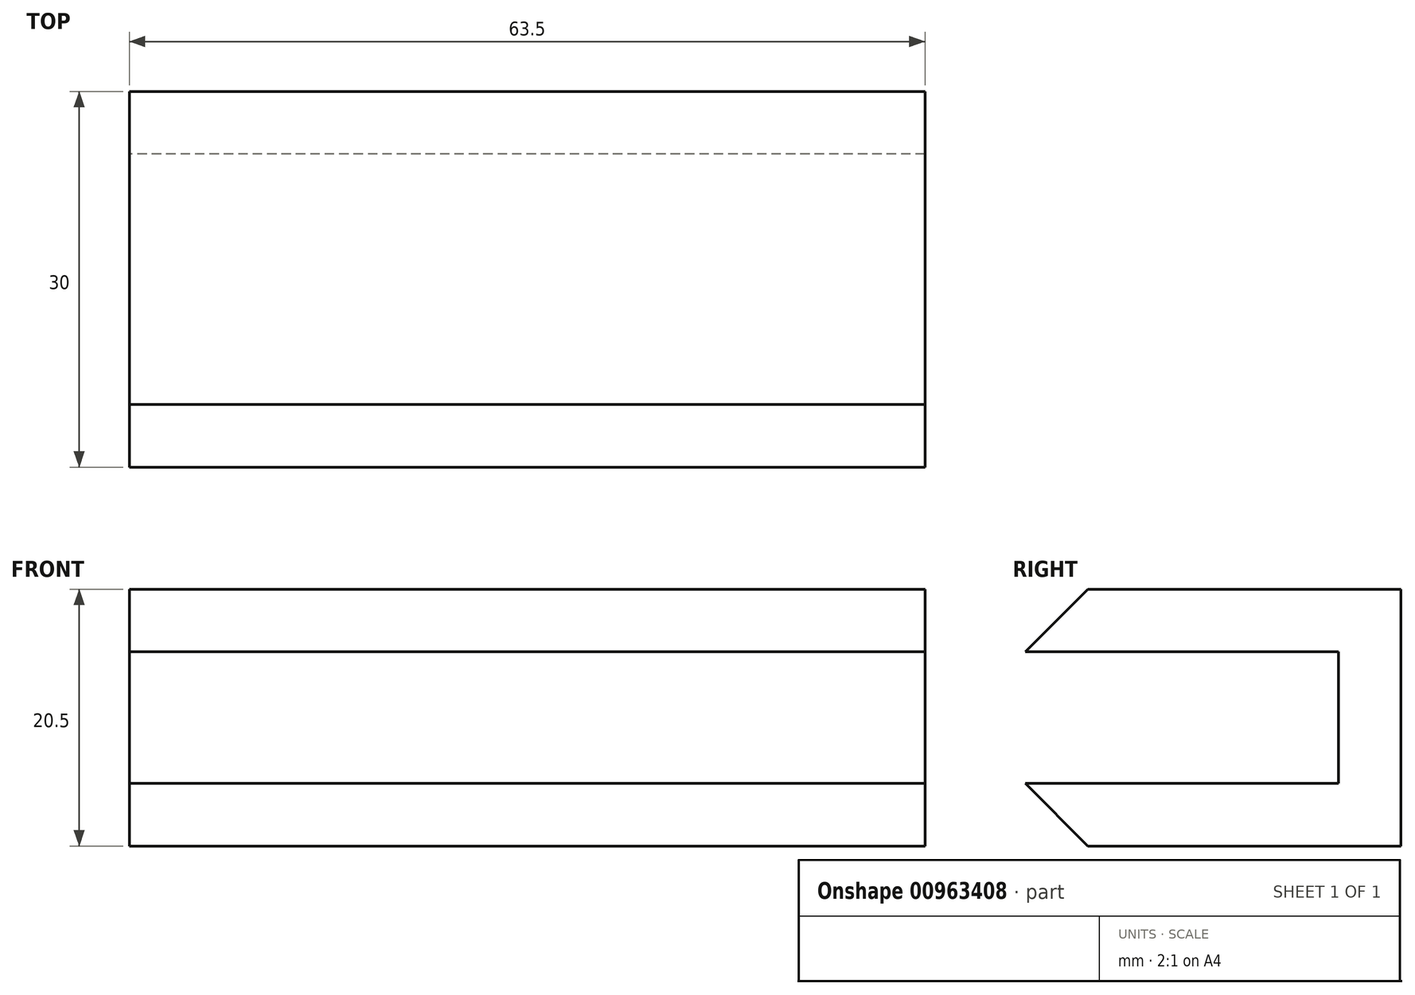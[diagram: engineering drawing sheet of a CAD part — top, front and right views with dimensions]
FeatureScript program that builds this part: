
annotation { "Feature Type Name" : "Feature", "Feature Type Description" : "" }
export const myFeature = defineFeature(function(context is Context, id is Id, definition is map)
    precondition{}
    {
        {
            var Q0;
            Q0=qCreatedBy(makeId("Top.planeOp"),FACE);
            var sketch = newSketch(context, id + "F0", { "sketchPlane" : qUnion([Q0])});
            skLineSegment(sketch, "E0.bottom", {"start": v(31.75, -2.5) * mm, "end": v(-31.75, -2.5) * mm});
            skLineSegment(sketch, "E0.top", {"start": v(31.75, 2.5) * mm, "end": v(-31.75, 2.5) * mm});
            skLineSegment(sketch, "E0.left", {"start": v(31.75, -2.5) * mm, "end": v(31.75, 2.5) * mm});
            skLineSegment(sketch, "E0.right", {"start": v(-31.75, -2.5) * mm, "end": v(-31.75, 2.5) * mm});
            skPoint(sketch, "E0.middle", {"position": v(0, 0) * mm});
            skSolve(sketch);
        }
        {
            var Q0;
            Q0=makeQuery(id+"F0.imprint","IMPRINT",FACE,{"disambiguationData":[TD([[makeQuery(id+"F0.imprint","IMPRINT",EDGE,{"derivedFrom":sQuery(id+"F0.wireOp",EDGE,"E0.bottom")}),-1.0]])]});
            extrude(context, id + "F1", {"entities" : qUnion([Q0]), "depth" : 10.5 * mm, "offsetDistance" : 25 * mm});
        }
        {
            var Q0;
            Q0=makeQuery(id+"F1.opExtrude","CAP_FACE",FACE,{"disambiguationData":[OSD([sQuery(id+"F0.wireOp",EDGE,"E0.bottom"),sQuery(id+"F0.wireOp",EDGE,"E0.top"),sQuery(id+"F0.wireOp",EDGE,"E0.left"),sQuery(id+"F0.wireOp",EDGE,"E0.right")])],"isStart":false});
            var sketch = newSketch(context, id + "F2", { "sketchPlane" : qUnion([Q0])});
            skLineSegment(sketch, "E1.bottom", {"start": v(-31.75, 2.5) * mm, "end": v(31.75, 2.5) * mm});
            skLineSegment(sketch, "E1.top", {"start": v(-31.75, -27.5) * mm, "end": v(31.75, -27.5) * mm});
            skLineSegment(sketch, "E1.left", {"start": v(-31.75, 2.5) * mm, "end": v(-31.75, -27.5) * mm});
            skLineSegment(sketch, "E1.right", {"start": v(31.75, 2.5) * mm, "end": v(31.75, -27.5) * mm});
            skSolve(sketch);
        }
        {
            var Q0;
            {var subQ0=sQuery(id+"F2.wireOp",EDGE,"E1.top");Q0=makeQuery(id+"F2.imprint","IMPRINT",FACE,{"disambiguationData":[TD([[makeQuery(id+"F2.imprint","IMPRINT",EDGE,{"derivedFrom":subQ0}),1.0]])]});}
            var Q1;
            {var subQ0=sQuery(id+"F2.wireOp",EDGE,"E1.bottom");Q1=makeQuery(id+"F2.imprint","IMPRINT",FACE,{"disambiguationData":[TD([[makeQuery(id+"F2.imprint","IMPRINT",EDGE,{"derivedFrom":subQ0}),1.0]])]});}
            extrude(context, id + "F3", {"entities" : qUnion([Q0, Q1]), "operationType" : NewBodyOperationType.ADD, "depth" : 5 * mm, "offsetDistance" : 25 * mm});
        }
        {
            var Q0;
            Q0=makeQuery(id+"F3.opExtrude","CAP_EDGE",EDGE,{"disambiguationData":[OSD([sQuery(id+"F2.wireOp",EDGE,"E1.top")])],"isStart":false});
            chamfer(context, id + "F4", {"entities" : qUnion([Q0]), "width" : 5 * mm, "tangentPropagation" : true});
        }
        {
            var Q0;
            Q0=makeQuery(id+"F1.opExtrude","CAP_FACE",FACE,{"disambiguationData":[OSD([sQuery(id+"F0.wireOp",EDGE,"E0.bottom"),sQuery(id+"F0.wireOp",EDGE,"E0.top"),sQuery(id+"F0.wireOp",EDGE,"E0.left"),sQuery(id+"F0.wireOp",EDGE,"E0.right")])],"isStart":true});
            var sketch = newSketch(context, id + "F5", { "sketchPlane" : qUnion([Q0])});
            skLineSegment(sketch, "E2.bottom", {"start": v(-31.75, -2.5) * mm, "end": v(31.75, -2.5) * mm});
            skLineSegment(sketch, "E2.top", {"start": v(-31.75, 27.5) * mm, "end": v(31.75, 27.5) * mm});
            skLineSegment(sketch, "E2.left", {"start": v(-31.75, -2.5) * mm, "end": v(-31.75, 27.5) * mm});
            skLineSegment(sketch, "E2.right", {"start": v(31.75, -2.5) * mm, "end": v(31.75, 27.5) * mm});
            skSolve(sketch);
        }
        {
            var Q0;
            {var subQ0=sQuery(id+"F5.wireOp",EDGE,"E2.bottom");Q0=makeQuery(id+"F5.imprint","IMPRINT",FACE,{"disambiguationData":[TD([[makeQuery(id+"F5.imprint","IMPRINT",EDGE,{"derivedFrom":subQ0}),-1.0]])]});}
            var Q1;
            {var subQ0=sQuery(id+"F5.wireOp",EDGE,"E2.top");Q1=makeQuery(id+"F5.imprint","IMPRINT",FACE,{"disambiguationData":[TD([[makeQuery(id+"F5.imprint","IMPRINT",EDGE,{"derivedFrom":subQ0}),-1.0]])]});}
            extrude(context, id + "F6", {"entities" : qUnion([Q0, Q1]), "operationType" : NewBodyOperationType.ADD, "depth" : 5 * mm, "offsetDistance" : 25 * mm});
        }
        {
            var Q0;
            Q0=makeQuery(id+"F6.opExtrude","CAP_EDGE",EDGE,{"disambiguationData":[OSD([sQuery(id+"F5.wireOp",EDGE,"E2.top")])],"isStart":false});
            chamfer(context, id + "F7", {"entities" : qUnion([Q0]), "width" : 5 * mm, "tangentPropagation" : true});
        }
    });
